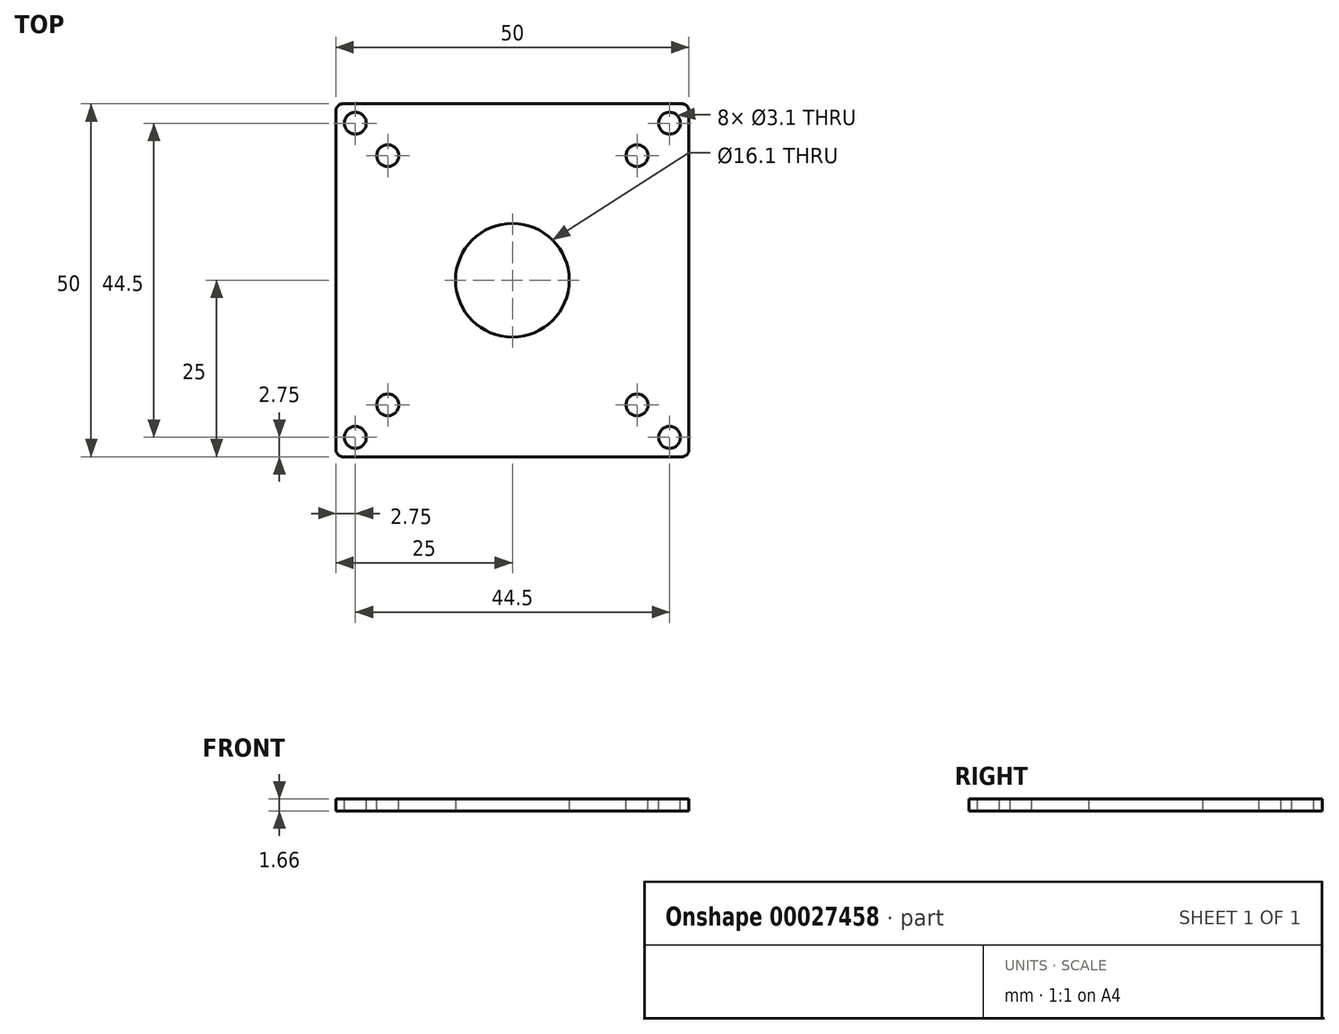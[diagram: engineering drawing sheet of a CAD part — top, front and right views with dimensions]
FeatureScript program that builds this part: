
annotation { "Feature Type Name" : "Feature", "Feature Type Description" : "" }
export const myFeature = defineFeature(function(context is Context, id is Id, definition is map)
    precondition{}
    {
        {
            var Q0;
            Q0=qCreatedBy(makeId("Top.planeOp"),FACE);
            var sketch = newSketch(context, id + "F0", { "sketchPlane" : qUnion([Q0])});
            skLineSegment(sketch, "E0.rect.bottom", {"start": v(25, -25) * mm, "end": v(-25, -25) * mm});
            skLineSegment(sketch, "E0.rect.top", {"start": v(25, 25) * mm, "end": v(-25, 25) * mm});
            skLineSegment(sketch, "E0.rect.left", {"start": v(25, -25) * mm, "end": v(25, 25) * mm});
            skLineSegment(sketch, "E0.rect.right", {"start": v(-25, -25) * mm, "end": v(-25, 25) * mm});
            skPoint(sketch, "E0.rect.middle", {"position": v(0, 0) * mm});
            skCircle(sketch, "E1", {"center": v(0, 0) * mm, "radius": 8.05 * mm});
            skSolve(sketch);
        }
        {
            var Q0;
            Q0 = qSketchRegion(id + "F0", true);
            extrude(context, id + "F1", {"entities" : qUnion([Q0]), "depth" : 1.66 * mm});
        }
        {
            var Q0;
            Q0=makeQuery(id+"F1.opExtrude","CAP_FACE",FACE,{"disambiguationData":[OSD([sQuery(id+"F0.wireOp",EDGE,"E0.rect.bottom"),sQuery(id+"F0.wireOp",EDGE,"E0.rect.top"),sQuery(id+"F0.wireOp",EDGE,"E0.rect.left"),sQuery(id+"F0.wireOp",EDGE,"E0.rect.right"),sQuery(id+"F0.wireOp",EDGE,"E1")])],"isStart":false});
            var sketch = newSketch(context, id + "F2", { "sketchPlane" : qUnion([Q0])});
            skCircle(sketch, "E2", {"center": v(-22.25, 22.25) * mm, "radius": 1.55 * mm});
            skCircle(sketch, "E3", {"center": v(22.25, 22.25) * mm, "radius": 1.55 * mm});
            skCircle(sketch, "E4", {"center": v(-22.25, -22.25) * mm, "radius": 1.55 * mm});
            skCircle(sketch, "E5", {"center": v(22.25, -22.25) * mm, "radius": 1.55 * mm});
            skLineSegment(sketch, "E6", {"start": v(-25, -25) * mm, "end": v(25, 25) * mm, "construction": true});
            skLineSegment(sketch, "E7", {"start": v(25, -25) * mm, "end": v(-25, 25) * mm, "construction": true});
            skCircle(sketch, "E8", {"center": v(-17.65, 17.65) * mm, "radius": 1.55 * mm});
            skCircle(sketch, "E9", {"center": v(17.65, 17.65) * mm, "radius": 1.55 * mm});
            skCircle(sketch, "E10", {"center": v(17.65, -17.65) * mm, "radius": 1.55 * mm});
            skCircle(sketch, "E11", {"center": v(-17.65, -17.65) * mm, "radius": 1.55 * mm});
            skLineSegment(sketch, "E12.0", {"start": v(25, 25) * mm, "end": v(-25, 25) * mm});
            skLineSegment(sketch, "E12.1", {"start": v(25, -25) * mm, "end": v(25, 25) * mm});
            skLineSegment(sketch, "E12.2", {"start": v(25, -25) * mm, "end": v(-25, -25) * mm});
            skLineSegment(sketch, "E12.3", {"start": v(-25, -25) * mm, "end": v(-25, 25) * mm});
            skSolve(sketch);
        }
        {
            var Q0;
            Q0=makeQuery(id+"F2.imprint","IMPRINT",FACE,{"disambiguationData":[TD([[makeQuery(id+"F2.imprint","IMPRINT",EDGE,{"derivedFrom":sQuery(id+"F2.wireOp",EDGE,"E2")}),1.0]])]});
            var Q1;
            Q1=makeQuery(id+"F2.imprint","IMPRINT",FACE,{"disambiguationData":[TD([[makeQuery(id+"F2.imprint","IMPRINT",EDGE,{"derivedFrom":sQuery(id+"F2.wireOp",EDGE,"E8")}),1.0]])]});
            var Q2;
            Q2=makeQuery(id+"F2.imprint","IMPRINT",FACE,{"disambiguationData":[TD([[makeQuery(id+"F2.imprint","IMPRINT",EDGE,{"derivedFrom":sQuery(id+"F2.wireOp",EDGE,"E11")}),1.0]])]});
            var Q3;
            Q3=makeQuery(id+"F2.imprint","IMPRINT",FACE,{"disambiguationData":[TD([[makeQuery(id+"F2.imprint","IMPRINT",EDGE,{"derivedFrom":sQuery(id+"F2.wireOp",EDGE,"E4")}),1.0]])]});
            var Q4;
            Q4=makeQuery(id+"F2.imprint","IMPRINT",FACE,{"disambiguationData":[TD([[makeQuery(id+"F2.imprint","IMPRINT",EDGE,{"derivedFrom":sQuery(id+"F2.wireOp",EDGE,"E5")}),1.0]])]});
            var Q5;
            Q5=makeQuery(id+"F2.imprint","IMPRINT",FACE,{"disambiguationData":[TD([[makeQuery(id+"F2.imprint","IMPRINT",EDGE,{"derivedFrom":sQuery(id+"F2.wireOp",EDGE,"E10")}),1.0]])]});
            var Q6;
            Q6=makeQuery(id+"F2.imprint","IMPRINT",FACE,{"disambiguationData":[TD([[makeQuery(id+"F2.imprint","IMPRINT",EDGE,{"derivedFrom":sQuery(id+"F2.wireOp",EDGE,"E9")}),1.0]])]});
            var Q7;
            Q7=makeQuery(id+"F2.imprint","IMPRINT",FACE,{"disambiguationData":[TD([[makeQuery(id+"F2.imprint","IMPRINT",EDGE,{"derivedFrom":sQuery(id+"F2.wireOp",EDGE,"E3")}),1.0]])]});
            extrude(context, id + "F3", {"entities" : qUnion([Q0, Q1, Q2, Q3, Q4, Q5, Q6, Q7]), "operationType" : NewBodyOperationType.REMOVE, "endBound" : BoundingType.THROUGH_ALL, "oppositeDirection" : true, "depth" : 25 * mm});
        }
        {
            var Q0;
            Q0=makeQuery(id+"F1.opExtrude","SWEPT_EDGE",EDGE,{"disambiguationData":[OSD([sQuery(id+"F0.wireOp",EDGE,"E0.rect.top"),sQuery(id+"F0.wireOp",EDGE,"E0.rect.right")])]});
            var Q1;
            Q1=makeQuery(id+"F1.opExtrude","SWEPT_EDGE",EDGE,{"disambiguationData":[OSD([sQuery(id+"F0.wireOp",EDGE,"E0.rect.bottom"),sQuery(id+"F0.wireOp",EDGE,"E0.rect.right")])]});
            var Q2;
            Q2=makeQuery(id+"F1.opExtrude","SWEPT_EDGE",EDGE,{"disambiguationData":[OSD([sQuery(id+"F0.wireOp",EDGE,"E0.rect.bottom"),sQuery(id+"F0.wireOp",EDGE,"E0.rect.left")])]});
            var Q3;
            Q3=makeQuery(id+"F1.opExtrude","SWEPT_EDGE",EDGE,{"disambiguationData":[OSD([sQuery(id+"F0.wireOp",EDGE,"E0.rect.top"),sQuery(id+"F0.wireOp",EDGE,"E0.rect.left")])]});
            fillet(context, id + "F4", {"entities" : qUnion([Q0, Q1, Q2, Q3]), "radius" : 1 * mm, "tangentPropagation" : true, "allowEdgeOverflow" : false});
        }
    });
